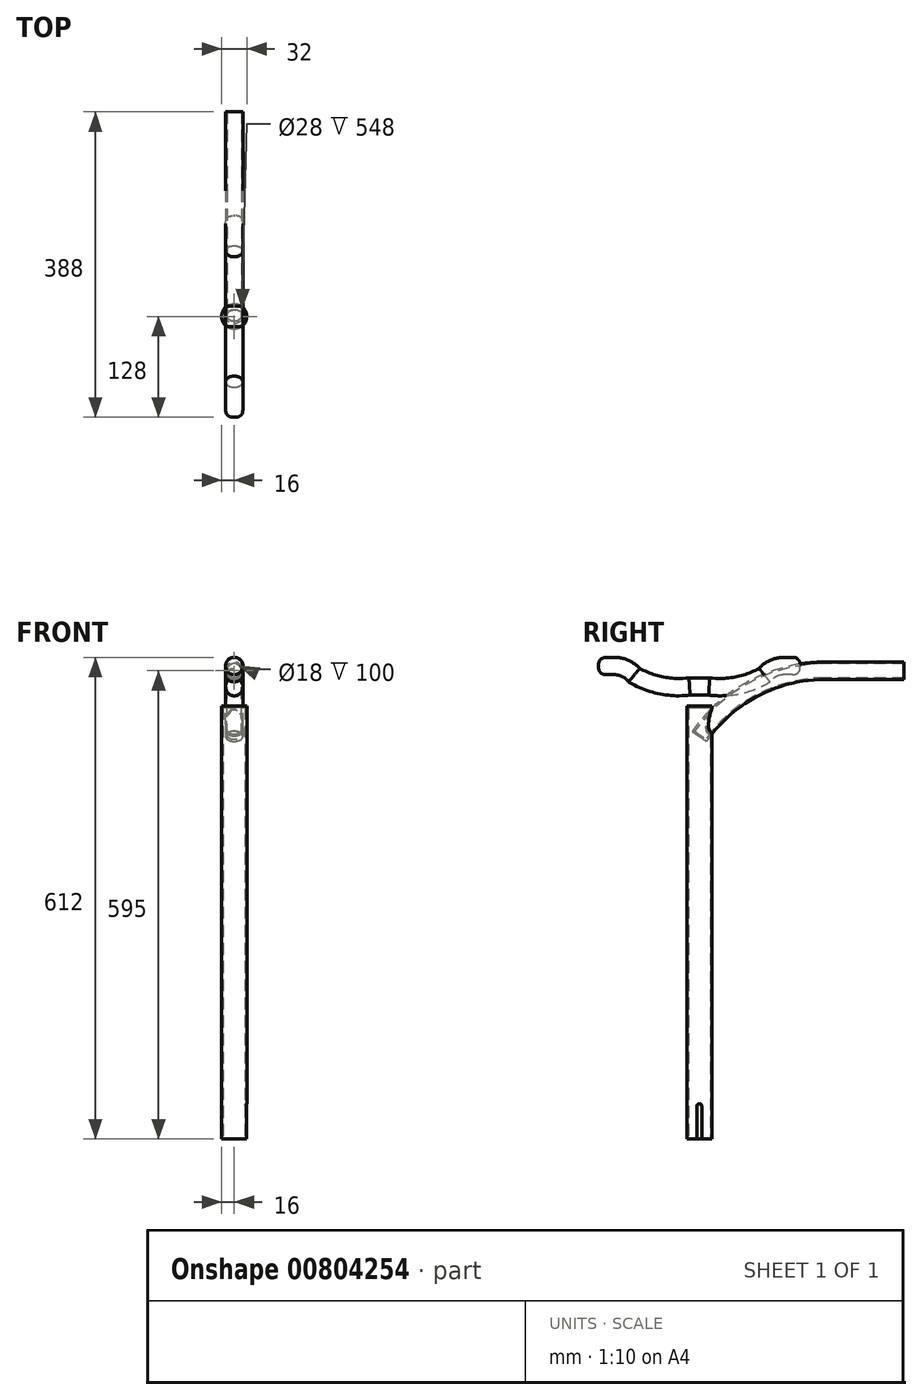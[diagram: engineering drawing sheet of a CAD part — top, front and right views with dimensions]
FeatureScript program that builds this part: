
annotation { "Feature Type Name" : "Feature", "Feature Type Description" : "" }
export const myFeature = defineFeature(function(context is Context, id is Id, definition is map)
    precondition{}
    {
        {
            var Q0;
            Q0=qCreatedBy(makeId("Top.planeOp"),FACE);
            var sketch = newSketch(context, id + "F0", { "sketchPlane" : qUnion([Q0])});
            skCircle(sketch, "E0", {"center": v(0, 0) * mm, "radius": 16 * mm});
            skSolve(sketch);
        }
        {
            var Q0;
            Q0 = qSketchRegion(id + "F0", true);
            extrude(context, id + "F1", {"entities" : qUnion([Q0]), "depth" : 550 * mm, "offsetDistance" : 25 * mm});
        }
        {
            var Q0;
            Q0=makeQuery(id+"F1.opExtrude","CAP_FACE",FACE,{"disambiguationData":[OSD([sQuery(id+"F0.wireOp",EDGE,"E0")])],"isStart":true});
            shell(context, id + "F2", {"entities" : qUnion([Q0]), "thickness" : 2 * mm});
        }
        {
            var Q0;
            Q0=qCreatedBy(makeId("Right.planeOp"),FACE);
            var sketch = newSketch(context, id + "F3", { "sketchPlane" : qUnion([Q0])});
            skLineSegment(sketch, "E1.bottom", {"start": v(3, 0) * mm, "end": v(-3, 0) * mm});
            skLineSegment(sketch, "E1.top", {"start": v(0, 45) * mm, "end": v(0, 45) * mm});
            skLineSegment(sketch, "E1.left", {"start": v(3, 0) * mm, "end": v(3, 42) * mm});
            skLineSegment(sketch, "E1.right", {"start": v(-3, 0) * mm, "end": v(-3, 42) * mm});
            skPoint(sketch, "E2.visualSharp", {"position": v(-3, 45) * mm});
            skArc(sketch, "E2.filletArc", {"start": v(0, 45) * mm, "mid": v(-2.12, 44.12) * mm, "end": v(-3, 42) * mm});
            skPoint(sketch, "E3.visualSharp", {"position": v(3, 45) * mm});
            skArc(sketch, "E3.filletArc", {"start": v(3, 42) * mm, "mid": v(2.12, 44.12) * mm, "end": v(0, 45) * mm});
            skSolve(sketch);
        }
        {
            var Q0;
            Q0 = qSketchRegion(id + "F3", true);
            extrude(context, id + "F4", {"entities" : qUnion([Q0]), "operationType" : NewBodyOperationType.REMOVE, "endBound" : BoundingType.THROUGH_ALL, "depth" : 25 * mm, "offsetDistance" : 25 * mm});
        }
        {
            var Q0;
            Q0=qCreatedBy(makeId("Right.planeOp"),FACE);
            var sketch = newSketch(context, id + "F5", { "sketchPlane" : qUnion([Q0])});
            skArc(sketch, "E4", {"start": v(160, 595) * mm, "mid": v(69.75, 572.86) * mm, "end": v(0, 511.47) * mm});
            skLineSegment(sketch, "E5", {"start": v(160, 595) * mm, "end": v(260, 595) * mm});
            skSolve(sketch);
        }
        {
            var Q0;
            Q0=sQuery(id+"F5.wireOp",VERTEX,"E5.end");
            var Q1;
            Q1=qCreatedBy(makeId("Front.planeOp"),FACE);
            cPlane(context, id + "F6", {"entities" : qUnion([Q0, Q1]), "cplaneType" : CPlaneType.PLANE_POINT, "offset" : 25 * mm, "width" : 150 * mm, "height" : 150 * mm});
        }
        {
            var Q0;
            Q0=qCreatedBy(id+"F6.planeOp",FACE);
            var sketch = newSketch(context, id + "F7", { "sketchPlane" : qUnion([Q0])});
            skCircle(sketch, "E6", {"center": v(0, 595) * mm, "radius": 11 * mm});
            skSolve(sketch);
        }
        {
            var Q0;
            Q0 = qSketchRegion(id + "F7", true);
            var Q1;
            Q1 = qConstructionFilter(qBodyType(qCreatedBy(id + "F5" ,EDGE), BodyType.WIRE), ConstructionObject.NO);
            sweep(context, id + "F8", {"operationType" : NewBodyOperationType.ADD, "profiles" : qUnion([Q0]), "path" : qUnion([Q1])});
        }
        {
            var Q0;
            Q0=makeQuery(id+"F8.opSweep","CAP_FACE",FACE,{"disambiguationData":[OSD([sQuery(id+"F5.wireOp",VERTEX,"E5.end"),sQuery(id+"F7.wireOp",EDGE,"E6")])],"isStart":true});
            shell(context, id + "F9", {"entities" : qUnion([Q0]), "thickness" : 2 * mm});
        }
        {
            var Q0;
            Q0=qCreatedBy(makeId("Right.planeOp"),FACE);
            var sketch = newSketch(context, id + "F10", { "sketchPlane" : qUnion([Q0])});
            skLineSegment(sketch, "E7", {"start": v(0, 525.22) * mm, "end": v(0, 586.9) * mm, "construction": true});
            skLineSegment(sketch, "E8", {"start": v(-128, 601) * mm, "end": v(-108, 601) * mm});
            skArc(sketch, "E9", {"start": v(-82.74, 589.34) * mm, "mid": v(-94.1, 597.95) * mm, "end": v(-108, 601) * mm});
            skArc(sketch, "E10", {"start": v(-82.74, 589.34) * mm, "mid": v(-48.8, 576.4) * mm, "end": v(-12.5, 575) * mm});
            skLineSegment(sketch, "E11", {"start": v(-12.5, 575) * mm, "end": v(0, 575) * mm});
            skLineSegment(sketch, "E12.MirrorCS", {"start": v(12.5, 575) * mm, "end": v(0, 575) * mm});
            skArc(sketch, "E13.MirrorCS", {"start": v(82.74, 589.34) * mm, "mid": v(48.8, 576.4) * mm, "end": v(12.5, 575) * mm});
            skArc(sketch, "E14.MirrorCS", {"start": v(82.74, 589.34) * mm, "mid": v(94.1, 597.95) * mm, "end": v(108, 601) * mm});
            skLineSegment(sketch, "E15.MirrorCS", {"start": v(128, 601) * mm, "end": v(108, 601) * mm});
            skSolve(sketch);
        }
        {
            var Q0;
            Q0=sQuery(id+"F10.wireOp",VERTEX,"E15.MirrorCS.start");
            var Q1;
            Q1=qCreatedBy(id+"F6.planeOp",FACE);
            cPlane(context, id + "F11", {"entities" : qUnion([Q0, Q1]), "cplaneType" : CPlaneType.PLANE_POINT, "offset" : 25 * mm, "width" : 150 * mm, "height" : 150 * mm});
        }
        {
            var Q0;
            Q0=qCreatedBy(id+"F11.planeOp",FACE);
            var sketch = newSketch(context, id + "F12", { "sketchPlane" : qUnion([Q0])});
            skCircle(sketch, "E16", {"center": v(0, 601) * mm, "radius": 11 * mm});
            skSolve(sketch);
        }
        {
            var Q0;
            Q0 = qSketchRegion(id + "F12", true);
            var Q1;
            Q1 = qConstructionFilter(qBodyType(qCreatedBy(id + "F10" ,EDGE), BodyType.WIRE), ConstructionObject.NO);
            sweep(context, id + "F13", {"profiles" : qUnion([Q0]), "path" : qUnion([Q1])});
        }
        {
            var Q0;
            Q0=makeQuery(id+"F13.opSweep","CAP_EDGE",EDGE,{"disambiguationData":[OSD([sQuery(id+"F10.wireOp",VERTEX,"E8.start"),sQuery(id+"F12.wireOp",EDGE,"E16")])],"isStart":false});
            var Q1;
            Q1=makeQuery(id+"F13.opSweep","CAP_EDGE",EDGE,{"disambiguationData":[OSD([sQuery(id+"F10.wireOp",VERTEX,"E15.MirrorCS.start"),sQuery(id+"F12.wireOp",EDGE,"E16")])],"isStart":true});
            fillet(context, id + "F14", {"entities" : qUnion([Q0, Q1]), "radius" : 10 * mm, "tangentPropagation" : true, "rho" : 0.5, "crossSection" : FilletCrossSection.CONIC, "allowEdgeOverflow" : false});
        }
    });
